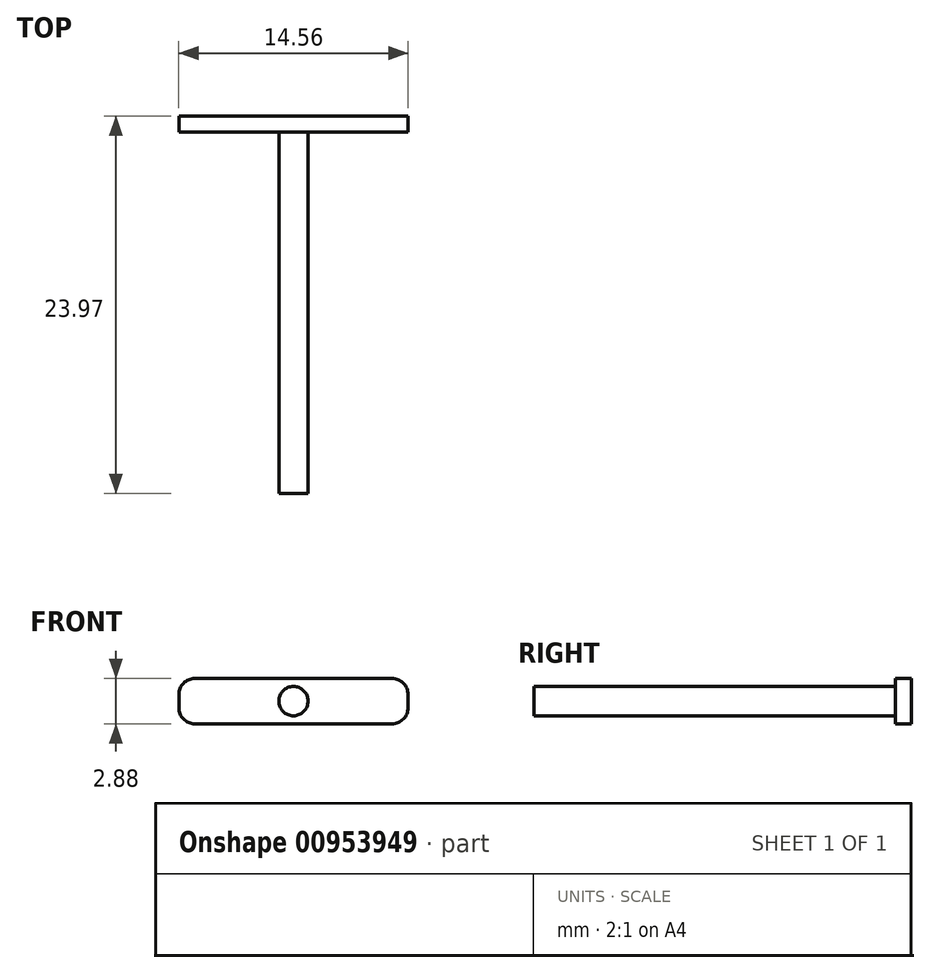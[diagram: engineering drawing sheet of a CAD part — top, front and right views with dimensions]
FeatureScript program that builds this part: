
annotation { "Feature Type Name" : "Feature", "Feature Type Description" : "" }
export const myFeature = defineFeature(function(context is Context, id is Id, definition is map)
    precondition{}
    {
        {
            var Q0;
            Q0=qCreatedBy(makeId("Top.planeOp"),FACE);
            var sketch = newSketch(context, id + "F0", { "sketchPlane" : qUnion([Q0])});
            skLineSegment(sketch, "E0.bottom", {"start": v(-62.68, 12.08) * mm, "end": v(-61.75, 12.08) * mm});
            skLineSegment(sketch, "E0.top", {"start": v(-62.68, -11.89) * mm, "end": v(-61.75, -11.89) * mm});
            skLineSegment(sketch, "E0.left", {"start": v(-62.68, 12.08) * mm, "end": v(-62.68, -11.89) * mm});
            skLineSegment(sketch, "E1", {"start": v(-61.75, 13.58) * mm, "end": v(-61.75, -11.89) * mm, "construction": true});
            skPoint(sketch, "E2.orphan", {"position": v(-61.75, 12.08) * mm});
            skPoint(sketch, "E0.right.start.orphan", {"position": v(-60.82, 12.08) * mm});
            skPoint(sketch, "E3.orphan", {"position": v(-60.82, -11.89) * mm});
            skLineSegment(sketch, "E4", {"start": v(-61.75, 12.08) * mm, "end": v(-61.75, -11.89) * mm});
            skSolve(sketch);
        }
        {
            var Q0;
            Q0=makeQuery(id+"F0.imprint","IMPRINT",FACE,{"disambiguationData":[TD([[makeQuery(id+"F0.imprint","IMPRINT",EDGE,{"derivedFrom":sQuery(id+"F0.wireOp",EDGE,"E0.bottom")}),-1.0]])]});
            var Q1;
            Q1=sQuery(id+"F0.wireOp",EDGE,"E1");
            revolve(context, id + "F1", {"surfaceOperationType" : NewSurfaceOperationType.NEW, "entities" : qUnion([Q0]), "axis" : qUnion([Q1]), "revolveType" : RevolveType.FULL});
        }
        {
            var Q0;
            Q0=makeQuery(id+"F1.opRevolve","SWEPT_FACE",FACE,{"disambiguationData":[OSD([sQuery(id+"F0.wireOp",EDGE,"E0.bottom")])]});
            var sketch = newSketch(context, id + "F2", { "sketchPlane" : qUnion([Q0])});
            skLineSegment(sketch, "E5.bottom", {"start": v(55.49, 1.44) * mm, "end": v(68.01, 1.44) * mm});
            skLineSegment(sketch, "E5.top", {"start": v(55.49, -1.44) * mm, "end": v(68.01, -1.44) * mm});
            skLineSegment(sketch, "E5.left", {"start": v(54.47, 0.42) * mm, "end": v(54.47, -0.42) * mm});
            skLineSegment(sketch, "E5.right", {"start": v(69.03, 0.42) * mm, "end": v(69.03, -0.42) * mm});
            skPoint(sketch, "E6.visualSharp", {"position": v(54.47, 1.44) * mm});
            skArc(sketch, "E6.filletArc", {"start": v(55.49, 1.44) * mm, "mid": v(54.77, 1.14) * mm, "end": v(54.47, 0.42) * mm});
            skPoint(sketch, "E7.visualSharp", {"position": v(54.47, -1.44) * mm});
            skArc(sketch, "E7.filletArc", {"start": v(54.47, -0.42) * mm, "mid": v(54.77, -1.14) * mm, "end": v(55.49, -1.44) * mm});
            skPoint(sketch, "E8.visualSharp", {"position": v(69.03, 1.44) * mm});
            skArc(sketch, "E8.filletArc", {"start": v(69.03, 0.42) * mm, "mid": v(68.73, 1.14) * mm, "end": v(68.01, 1.44) * mm});
            skPoint(sketch, "E9.visualSharp", {"position": v(69.03, -1.44) * mm});
            skArc(sketch, "E9.filletArc", {"start": v(68.01, -1.44) * mm, "mid": v(68.73, -1.14) * mm, "end": v(69.03, -0.42) * mm});
            skSolve(sketch);
        }
        {
            var Q0;
            Q0=makeQuery(id+"F2.imprint","IMPRINT",FACE,{"disambiguationData":[TD([[makeQuery(id+"F2.imprint","IMPRINT",EDGE,{"derivedFrom":sQuery(id+"F2.wireOp",EDGE,"E5.bottom")}),-1.0]])]});
            extrude(context, id + "F3", {"entities" : qUnion([Q0]), "operationType" : NewBodyOperationType.ADD, "depth" : -1.02 * mm, "offsetDistance" : 25.4 * mm});
        }
    });
